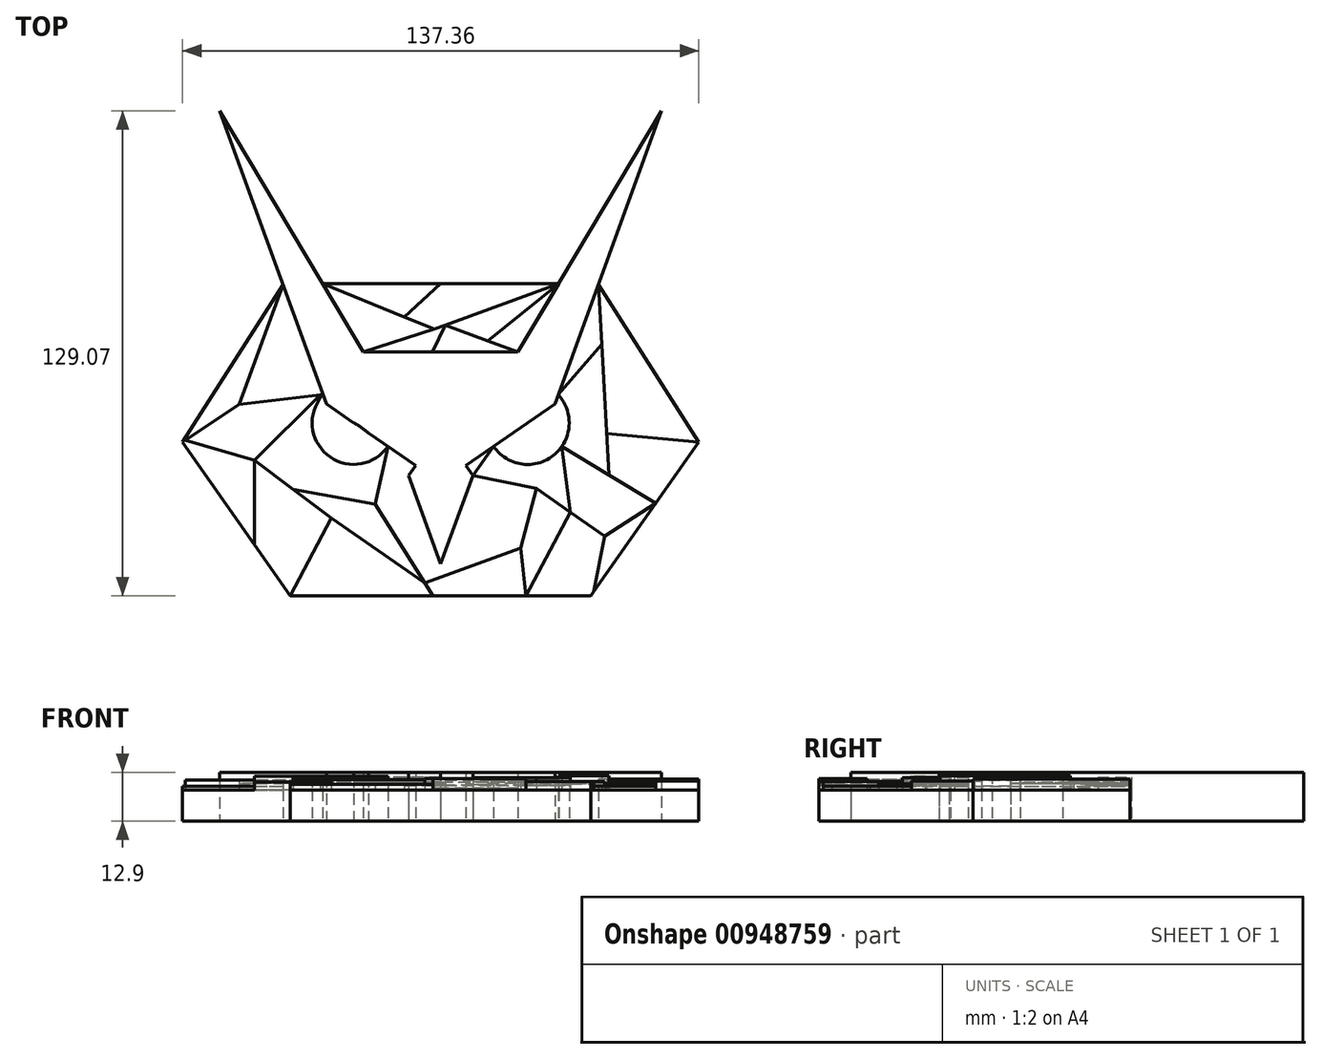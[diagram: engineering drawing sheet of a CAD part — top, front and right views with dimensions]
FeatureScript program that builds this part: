
annotation { "Feature Type Name" : "Feature", "Feature Type Description" : "" }
export const myFeature = defineFeature(function(context is Context, id is Id, definition is map)
    precondition{}
    {
        {
            var Q0;
            Q0=qCreatedBy(makeId("Top.planeOp"),FACE);
            var sketch = newSketch(context, id + "F0", { "sketchPlane" : qUnion([Q0])});
            skLineSegment(sketch, "E0", {"start": v(-40.57, 106.01) * mm, "end": v(-40.57, -104.1) * mm});
            skLineSegment(sketch, "E1", {"start": v(-40.57, 0) * mm, "end": v(-80.57, 0) * mm});
            skPoint(sketch, "E1.startSnap0", {"position": v(-40.57, 0.95) * mm});
            skLineSegment(sketch, "E2", {"start": v(-80.57, 0) * mm, "end": v(-109.25, 40.96) * mm});
            skLineSegment(sketch, "E3", {"start": v(-109.25, 40.96) * mm, "end": v(-82.39, 83.13) * mm});
            skLineSegment(sketch, "E4.MirrorCS", {"start": v(-40.57, 0) * mm, "end": v(-0.57, 0) * mm});
            skLineSegment(sketch, "E5.MirrorCS", {"start": v(-0.57, 0) * mm, "end": v(28.1, 40.96) * mm});
            skLineSegment(sketch, "E6.MirrorCS", {"start": v(28.1, 40.96) * mm, "end": v(1.24, 83.13) * mm});
            skLineSegment(sketch, "E7", {"start": v(-40.57, 0) * mm, "end": v(-40.57, 8.54) * mm});
            skLineSegment(sketch, "E8", {"start": v(-40.57, 8.54) * mm, "end": v(-49.12, 32.03) * mm});
            skLineSegment(sketch, "E9", {"start": v(-49.12, 32.03) * mm, "end": v(-45.4, 37.35) * mm});
            skLineSegment(sketch, "E10", {"start": v(-47.26, 34.7) * mm, "end": v(-71, 51.04) * mm});
            skLineSegment(sketch, "E11", {"start": v(-71, 51.04) * mm, "end": v(-99.4, 129.07) * mm});
            skLineSegment(sketch, "E12", {"start": v(-99.4, 129.07) * mm, "end": v(-61.13, 64.93) * mm});
            skLineSegment(sketch, "E13", {"start": v(-61.13, 64.93) * mm, "end": v(-40.57, 64.93) * mm});
            skLineSegment(sketch, "E14", {"start": v(-47.26, 34.7) * mm, "end": v(-59.61, 43.2) * mm});
            skLineSegment(sketch, "E15", {"start": v(-59.61, 43.2) * mm, "end": v(-63.73, 46.04) * mm});
            skFitSpline(sketch, "E16", {"points": [v(-63.73, 46.04) * mm, v(-55.85, 40.6) * mm], "startDerivative": vector(8.61, -4.18) * mm, "endDerivative": vector(8.61, -4.18) * mm});
            skArc(sketch, "E17", {"start": v(-72.82, 52.3) * mm, "mid": v(-70, 36.95) * mm, "end": v(-54.64, 39.77) * mm});
            skLineSegment(sketch, "E18", {"start": v(-71.99, 83.13) * mm, "end": v(-40.57, 83.13) * mm});
            skLineSegment(sketch, "E19", {"start": v(-72.82, 52.3) * mm, "end": v(-71.93, 53.6) * mm});
            skLineSegment(sketch, "E20.MirrorCS", {"start": v(-20.02, 64.93) * mm, "end": v(-40.57, 64.93) * mm});
            skLineSegment(sketch, "E21.MirrorCS", {"start": v(18.25, 129.07) * mm, "end": v(-20.02, 64.93) * mm});
            skLineSegment(sketch, "E22.MirrorCS", {"start": v(-9.16, 83.13) * mm, "end": v(-40.57, 83.13) * mm});
            skLineSegment(sketch, "E23.MirrorCS", {"start": v(-10.15, 51.04) * mm, "end": v(18.25, 129.07) * mm});
            skLineSegment(sketch, "E24.MirrorCS", {"start": v(-33.89, 34.7) * mm, "end": v(-10.15, 51.04) * mm});
            skArc(sketch, "E25.MirrorCS", {"start": v(-8.33, 52.3) * mm, "mid": v(-11.15, 36.95) * mm, "end": v(-26.5, 39.77) * mm});
            skLineSegment(sketch, "E26.MirrorCS", {"start": v(-8.33, 52.3) * mm, "end": v(-9.22, 53.6) * mm});
            skLineSegment(sketch, "E27.MirrorCS", {"start": v(-32.02, 32.03) * mm, "end": v(-35.75, 37.35) * mm});
            skLineSegment(sketch, "E28.MirrorCS", {"start": v(-40.57, 8.54) * mm, "end": v(-32.02, 32.03) * mm});
            skSolve(sketch);
        }
        {
            var Q0;
            {var subQ5=sQuery(id+"F0.wireOp",EDGE,"E1");Q0=makeQuery(id+"F0.imprint","IMPRINT",FACE,{"disambiguationData":[TD([[makeQuery(id+"F0.imprint","IMPRINT",EDGE,{"derivedFrom":subQ5}),-1.0]])]});}
            var Q1;
            {var subQ4=sQuery(id+"F0.wireOp",EDGE,"E4.MirrorCS");Q1=makeQuery(id+"F0.imprint","IMPRINT",FACE,{"disambiguationData":[TD([[makeQuery(id+"F0.imprint","IMPRINT",EDGE,{"derivedFrom":subQ4}),1.0]])]});}
            var Q2;
            {var subQ0=sQuery(id+"F0.wireOp",EDGE,"E20.MirrorCS");Q2=makeQuery(id+"F0.imprint","IMPRINT",FACE,{"disambiguationData":[TD([[makeQuery(id+"F0.imprint","IMPRINT",EDGE,{"derivedFrom":subQ0}),-1.0]])]});}
            var Q3;
            {var subQ0=sQuery(id+"F0.wireOp",EDGE,"E13");Q3=makeQuery(id+"F0.imprint","IMPRINT",FACE,{"disambiguationData":[TD([[makeQuery(id+"F0.imprint","IMPRINT",EDGE,{"derivedFrom":subQ0}),1.0]])]});}
            extrude(context, id + "F1", {"entities" : qUnion([Q0, Q1, Q2, Q3]), "depth" : 8.3 * mm, "offsetDistance" : 25 * mm});
        }
        {
            var Q0;
            {var subQ14=sQuery(id+"F0.wireOp",EDGE,"E8");Q0=makeQuery(id+"F0.imprint","IMPRINT",FACE,{"disambiguationData":[TD([[makeQuery(id+"F0.imprint","IMPRINT",EDGE,{"derivedFrom":subQ14}),-1.0]])]});}
            var Q1;
            {var subQ12=sQuery(id+"F0.wireOp",EDGE,"E20.MirrorCS");Q1=makeQuery(id+"F0.imprint","IMPRINT",FACE,{"disambiguationData":[TD([[makeQuery(id+"F0.imprint","IMPRINT",EDGE,{"derivedFrom":subQ12}),1.0]])]});}
            extrude(context, id + "F2", {"entities" : qUnion([Q0, Q1]), "depth" : 12.9 * mm, "offsetDistance" : 25 * mm});
        }
        {
            var Q0;
            Q0=makeQuery(id+"F1.opExtrude","CAP_FACE",FACE,{"disambiguationData":[OSD([sQuery(id+"F0.wireOp",EDGE,"E1"),sQuery(id+"F0.wireOp",EDGE,"E2"),sQuery(id+"F0.wireOp",EDGE,"E3"),sQuery(id+"F0.wireOp",EDGE,"E4.MirrorCS"),sQuery(id+"F0.wireOp",EDGE,"E5.MirrorCS"),sQuery(id+"F0.wireOp",EDGE,"E6.MirrorCS"),sQuery(id+"F0.wireOp",EDGE,"E8"),sQuery(id+"F0.wireOp",EDGE,"E9"),sQuery(id+"F0.wireOp",EDGE,"E10"),sQuery(id+"F0.wireOp",EDGE,"E11"),sQuery(id+"F0.wireOp",EDGE,"E17"),sQuery(id+"F0.wireOp",EDGE,"E19"),sQuery(id+"F0.wireOp",EDGE,"E23.MirrorCS"),sQuery(id+"F0.wireOp",EDGE,"E24.MirrorCS"),sQuery(id+"F0.wireOp",EDGE,"E25.MirrorCS"),sQuery(id+"F0.wireOp",EDGE,"E26.MirrorCS"),sQuery(id+"F0.wireOp",EDGE,"E27.MirrorCS"),sQuery(id+"F0.wireOp",EDGE,"E28.MirrorCS")])],"isStart":false});
            var sketch = newSketch(context, id + "F3", { "sketchPlane" : qUnion([Q0])});
            skLineSegment(sketch, "E29", {"start": v(-80.57, 0) * mm, "end": v(-69.7, 20.68) * mm});
            skLineSegment(sketch, "E30", {"start": v(-69.7, 20.68) * mm, "end": v(-90.08, 36.07) * mm});
            skLineSegment(sketch, "E31", {"start": v(-71.93, 53.6) * mm, "end": v(-94.27, 50.91) * mm});
            skLineSegment(sketch, "E32", {"start": v(-94.27, 50.91) * mm, "end": v(-82.57, 82.84) * mm});
            skLineSegment(sketch, "E33", {"start": v(-94.27, 50.91) * mm, "end": v(-108.58, 41.4) * mm});
            skLineSegment(sketch, "E34", {"start": v(-90.08, 36.07) * mm, "end": v(-90.08, 13.58) * mm});
            skLineSegment(sketch, "E35", {"start": v(-79.9, 28.37) * mm, "end": v(-58.07, 24.4) * mm});
            skLineSegment(sketch, "E36", {"start": v(-58.07, 24.4) * mm, "end": v(-54.64, 39.77) * mm});
            skLineSegment(sketch, "E37", {"start": v(-58.07, 24.4) * mm, "end": v(-42.67, 0) * mm});
            skLineSegment(sketch, "E38", {"start": v(-69.7, 20.68) * mm, "end": v(-44.85, 3.46) * mm});
            skLineSegment(sketch, "E39", {"start": v(-44.85, 3.46) * mm, "end": v(-19.23, 12.78) * mm});
            skLineSegment(sketch, "E40", {"start": v(-19.23, 12.78) * mm, "end": v(-15.06, 28.57) * mm});
            skLineSegment(sketch, "E41", {"start": v(-15.06, 28.57) * mm, "end": v(-32.02, 32.03) * mm});
            skLineSegment(sketch, "E42", {"start": v(-32.02, 32.03) * mm, "end": v(-26.5, 39.77) * mm});
            skLineSegment(sketch, "E43", {"start": v(-15.06, 28.57) * mm, "end": v(3.04, 15.9) * mm});
            skLineSegment(sketch, "E44", {"start": v(3.04, 15.9) * mm, "end": v(16.68, 24.64) * mm});
            skLineSegment(sketch, "E45", {"start": v(16.68, 24.64) * mm, "end": v(-8.33, 39.77) * mm});
            skLineSegment(sketch, "E46", {"start": v(-8.33, 39.77) * mm, "end": v(-6, 22.23) * mm});
            skLineSegment(sketch, "E47", {"start": v(4.18, 32.2) * mm, "end": v(1.43, 82.84) * mm});
            skLineSegment(sketch, "E48", {"start": v(3.58, 43.24) * mm, "end": v(28.1, 40.96) * mm});
            skLineSegment(sketch, "E49", {"start": v(2.3, 66.9) * mm, "end": v(-9.22, 53.6) * mm});
            skLineSegment(sketch, "E50", {"start": v(3.04, 15.9) * mm, "end": v(0, 0) * mm});
            skLineSegment(sketch, "E51", {"start": v(-6, 22.23) * mm, "end": v(-17.88, 0) * mm});
            skLineSegment(sketch, "E52", {"start": v(-17.88, 0) * mm, "end": v(-19.23, 12.78) * mm});
            skLineSegment(sketch, "E53", {"start": v(-90.08, 36.07) * mm, "end": v(-108.58, 41.4) * mm});
            skLineSegment(sketch, "E54", {"start": v(-90.08, 36.07) * mm, "end": v(-72.62, 53.51) * mm});
            skSolve(sketch);
        }
        {
            var Q0;
            {var subQ3=sQuery(id+"F3.wireOp",EDGE,"E29");Q0=makeQuery(id+"F3.imprint","IMPRINT",FACE,{"disambiguationData":[TD([[makeQuery(id+"F3.imprint","IMPRINT",EDGE,{"derivedFrom":subQ3}),1.0]])]});}
            extrude(context, id + "F4", {"entities" : qUnion([Q0]), "operationType" : NewBodyOperationType.ADD, "depth" : 2.1 * mm, "offsetDistance" : 25 * mm});
        }
        {
            var Q0;
            Q0=makeQuery(id+"F3.imprint","IMPRINT",FACE,{"disambiguationData":[TD([[makeQuery(id+"F3.imprint","IMPRINT",EDGE,{"derivedFrom":sQuery(id+"F3.wireOp",EDGE,"E31")}),-1.0]])]});
            extrude(context, id + "F5", {"entities" : qUnion([Q0]), "depth" : 1.7 * mm, "offsetDistance" : 25 * mm});
        }
        {
            var Q0;
            Q0=makeQuery(id+"F3.imprint","IMPRINT",FACE,{"disambiguationData":[TD([[makeQuery(id+"F3.imprint","IMPRINT",EDGE,{"derivedFrom":sQuery(id+"F3.wireOp",EDGE,"E32")}),1.0]])]});
            extrude(context, id + "F6", {"entities" : qUnion([Q0]), "depth" : 0.9 * mm, "offsetDistance" : 25 * mm});
        }
        {
            var Q0;
            {var subQ0=sQuery(id+"F3.wireOp",EDGE,"E33");Q0=makeQuery(id+"F3.imprint","IMPRINT",FACE,{"disambiguationData":[TD([[makeQuery(id+"F3.imprint","IMPRINT",EDGE,{"derivedFrom":subQ0}),1.0]])]});}
            extrude(context, id + "F7", {"entities" : qUnion([Q0]), "depth" : 2.6 * mm, "offsetDistance" : 25 * mm});
        }
        {
            var Q0;
            {var subQ0=sQuery(id+"F3.wireOp",EDGE,"E35");Q0=makeQuery(id+"F3.imprint","IMPRINT",FACE,{"disambiguationData":[TD([[makeQuery(id+"F3.imprint","IMPRINT",EDGE,{"derivedFrom":subQ0}),1.0]])]});}
            extrude(context, id + "F8", {"entities" : qUnion([Q0]), "depth" : 3.6 * mm, "offsetDistance" : 25 * mm});
        }
        {
            var Q0;
            {var subQ2=sQuery(id+"F3.wireOp",EDGE,"E35");Q0=makeQuery(id+"F3.imprint","IMPRINT",FACE,{"disambiguationData":[TD([[makeQuery(id+"F3.imprint","IMPRINT",EDGE,{"derivedFrom":subQ2}),-1.0]])]});}
            extrude(context, id + "F9", {"entities" : qUnion([Q0]), "depth" : 2.7 * mm, "offsetDistance" : 25 * mm});
        }
        {
            var Q0;
            {var subQ0=sQuery(id+"F3.wireOp",EDGE,"E29");Q0=makeQuery(id+"F3.imprint","IMPRINT",FACE,{"disambiguationData":[TD([[makeQuery(id+"F3.imprint","IMPRINT",EDGE,{"derivedFrom":subQ0}),-1.0]])]});}
            extrude(context, id + "F10", {"entities" : qUnion([Q0]), "depth" : 1.5 * mm, "offsetDistance" : 25 * mm});
        }
        {
            var Q0;
            {var subQ2=sQuery(id+"F3.wireOp",EDGE,"E36");Q0=makeQuery(id+"F3.imprint","IMPRINT",FACE,{"disambiguationData":[TD([[makeQuery(id+"F3.imprint","IMPRINT",EDGE,{"derivedFrom":subQ2}),-1.0]])]});}
            extrude(context, id + "F11", {"entities" : qUnion([Q0]), "depth" : 2.1 * mm, "offsetDistance" : 25 * mm});
        }
        {
            var Q0;
            {var subQ3=sQuery(id+"F3.wireOp",EDGE,"E39");Q0=makeQuery(id+"F3.imprint","IMPRINT",FACE,{"disambiguationData":[TD([[makeQuery(id+"F3.imprint","IMPRINT",EDGE,{"derivedFrom":subQ3}),-1.0]])]});}
            extrude(context, id + "F12", {"entities" : qUnion([Q0]), "depth" : 3 * mm, "offsetDistance" : 25 * mm});
        }
        {
            var Q0;
            {var subQ0=sQuery(id+"F3.wireOp",EDGE,"E40");Q0=makeQuery(id+"F3.imprint","IMPRINT",FACE,{"disambiguationData":[TD([[makeQuery(id+"F3.imprint","IMPRINT",EDGE,{"derivedFrom":subQ0}),-1.0]])]});}
            extrude(context, id + "F13", {"entities" : qUnion([Q0]), "depth" : 1.2 * mm, "offsetDistance" : 25 * mm});
        }
        {
            var Q0;
            {var subQ4=sQuery(id+"F3.wireOp",EDGE,"E41");Q0=makeQuery(id+"F3.imprint","IMPRINT",FACE,{"disambiguationData":[TD([[makeQuery(id+"F3.imprint","IMPRINT",EDGE,{"derivedFrom":subQ4}),-1.0]])]});}
            extrude(context, id + "F14", {"entities" : qUnion([Q0]), "depth" : 3.2 * mm, "offsetDistance" : 25 * mm});
        }
        {
            var Q0;
            Q0=makeQuery(id+"F3.imprint","IMPRINT",FACE,{"disambiguationData":[TD([[makeQuery(id+"F3.imprint","IMPRINT",EDGE,{"derivedFrom":sQuery(id+"F3.wireOp",EDGE,"E42")}),1.0]])]});
            extrude(context, id + "F15", {"entities" : qUnion([Q0]), "depth" : 1.5 * mm, "offsetDistance" : 25 * mm});
        }
        {
            var Q0;
            {var subQ3=sQuery(id+"F3.wireOp",EDGE,"E51");Q0=makeQuery(id+"F3.imprint","IMPRINT",FACE,{"disambiguationData":[TD([[makeQuery(id+"F3.imprint","IMPRINT",EDGE,{"derivedFrom":subQ3}),1.0]])]});}
            extrude(context, id + "F16", {"entities" : qUnion([Q0]), "depth" : 2.2 * mm, "offsetDistance" : 25 * mm});
        }
        {
            var Q0;
            {var subQ3=sQuery(id+"F3.wireOp",EDGE,"E44");Q0=makeQuery(id+"F3.imprint","IMPRINT",FACE,{"disambiguationData":[TD([[makeQuery(id+"F3.imprint","IMPRINT",EDGE,{"derivedFrom":subQ3}),1.0]])]});}
            extrude(context, id + "F17", {"entities" : qUnion([Q0]), "depth" : 1.6 * mm, "offsetDistance" : 25 * mm});
        }
        {
            var Q0;
            {var subQ0=sQuery(id+"F3.wireOp",EDGE,"E44");Q0=makeQuery(id+"F3.imprint","IMPRINT",FACE,{"disambiguationData":[TD([[makeQuery(id+"F3.imprint","IMPRINT",EDGE,{"derivedFrom":subQ0}),-1.0]])]});}
            extrude(context, id + "F18", {"entities" : qUnion([Q0]), "depth" : 1 * mm, "offsetDistance" : 25 * mm});
        }
        {
            var Q0;
            {var subQ0=sQuery(id+"F3.wireOp",EDGE,"E49");Q0=makeQuery(id+"F3.imprint","IMPRINT",FACE,{"disambiguationData":[TD([[makeQuery(id+"F3.imprint","IMPRINT",EDGE,{"derivedFrom":subQ0}),1.0]])]});}
            extrude(context, id + "F19", {"entities" : qUnion([Q0]), "depth" : 3.7 * mm, "offsetDistance" : 25 * mm});
        }
        {
            var Q0;
            {var subQ5=sQuery(id+"F3.wireOp",EDGE,"E48");Q0=makeQuery(id+"F3.imprint","IMPRINT",FACE,{"disambiguationData":[TD([[makeQuery(id+"F3.imprint","IMPRINT",EDGE,{"derivedFrom":subQ5}),-1.0]])]});}
            extrude(context, id + "F20", {"entities" : qUnion([Q0]), "depth" : 2.4 * mm, "offsetDistance" : 25 * mm});
        }
        {
            var Q0;
            {var subQ0=sQuery(id+"F3.wireOp",EDGE,"E48");Q0=makeQuery(id+"F3.imprint","IMPRINT",FACE,{"disambiguationData":[TD([[makeQuery(id+"F3.imprint","IMPRINT",EDGE,{"derivedFrom":subQ0}),1.0]])]});}
            extrude(context, id + "F21", {"entities" : qUnion([Q0]), "depth" : 2.9 * mm, "offsetDistance" : 25 * mm});
        }
        {
            var Q0;
            {var subQ2=sQuery(id+"F3.wireOp",EDGE,"E49");Q0=makeQuery(id+"F3.imprint","IMPRINT",FACE,{"disambiguationData":[TD([[makeQuery(id+"F3.imprint","IMPRINT",EDGE,{"derivedFrom":subQ2}),-1.0]])]});}
            extrude(context, id + "F22", {"entities" : qUnion([Q0]), "depth" : 2.03 * mm, "offsetDistance" : 25 * mm});
        }
        {
            var Q0;
            Q0=makeQuery(id+"F1.opExtrude","CAP_FACE",FACE,{"disambiguationData":[OSD([sQuery(id+"F0.wireOp",EDGE,"E12"),sQuery(id+"F0.wireOp",EDGE,"E13"),sQuery(id+"F0.wireOp",EDGE,"E18"),sQuery(id+"F0.wireOp",EDGE,"E20.MirrorCS"),sQuery(id+"F0.wireOp",EDGE,"E21.MirrorCS"),sQuery(id+"F0.wireOp",EDGE,"E22.MirrorCS")])],"isStart":false});
            var sketch = newSketch(context, id + "F23", { "sketchPlane" : qUnion([Q0])});
            skLineSegment(sketch, "E55", {"start": v(-61.13, 64.93) * mm, "end": v(-39.3, 72) * mm});
            skLineSegment(sketch, "E56", {"start": v(-39.3, 72) * mm, "end": v(-20.02, 64.93) * mm});
            skLineSegment(sketch, "E57", {"start": v(-28.01, 67.86) * mm, "end": v(-9.16, 83.13) * mm});
            skLineSegment(sketch, "E58", {"start": v(-42.31, 71.02) * mm, "end": v(-71.99, 83.13) * mm});
            skLineSegment(sketch, "E59", {"start": v(-50.23, 74.25) * mm, "end": v(-40.57, 83.13) * mm});
            skLineSegment(sketch, "E60", {"start": v(-39.3, 72) * mm, "end": v(-9.16, 83.13) * mm});
            skLineSegment(sketch, "E61", {"start": v(-39.3, 72) * mm, "end": v(-42.73, 64.93) * mm});
            skSolve(sketch);
        }
        {
            var Q0;
            {var subQ1=makeQuery(id+"F1.opExtrude","CAP_EDGE",EDGE,{"disambiguationData":[OSD([sQuery(id+"F0.wireOp",EDGE,"E12")])],"isStart":false});Q0=makeQuery(id+"F23.imprint","IMPRINT",FACE,{"disambiguationData":[TD([[makeQuery(id+"F23.imprint","IMPRINT",EDGE,{"derivedFrom":subQ1}),1.0]])]});}
            extrude(context, id + "F24", {"entities" : qUnion([Q0]), "depth" : 2.1 * mm, "offsetDistance" : 25 * mm});
        }
        {
            var Q0;
            {var subQ3=sQuery(id+"F23.wireOp",EDGE,"E59");Q0=makeQuery(id+"F23.imprint","IMPRINT",FACE,{"disambiguationData":[TD([[makeQuery(id+"F23.imprint","IMPRINT",EDGE,{"derivedFrom":subQ3}),1.0]])]});}
            extrude(context, id + "F25", {"entities" : qUnion([Q0]), "depth" : 3.4 * mm, "offsetDistance" : 25 * mm});
        }
        {
            var Q0;
            {var subQ1=sQuery(id+"F23.wireOp",EDGE,"E59");Q0=makeQuery(id+"F23.imprint","IMPRINT",FACE,{"disambiguationData":[TD([[makeQuery(id+"F23.imprint","IMPRINT",EDGE,{"derivedFrom":subQ1}),-1.0]])]});}
            extrude(context, id + "F26", {"entities" : qUnion([Q0]), "depth" : 1.2 * mm, "offsetDistance" : 25 * mm});
        }
        {
            var Q0;
            {var subQ4=sQuery(id+"F23.wireOp",EDGE,"E61");Q0=makeQuery(id+"F23.imprint","IMPRINT",FACE,{"disambiguationData":[TD([[makeQuery(id+"F23.imprint","IMPRINT",EDGE,{"derivedFrom":subQ4}),-1.0]])]});}
            extrude(context, id + "F27", {"entities" : qUnion([Q0]), "depth" : 1.6 * mm, "offsetDistance" : 25 * mm});
        }
        {
            var Q0;
            {var subQ0=sQuery(id+"F23.wireOp",EDGE,"E61");Q0=makeQuery(id+"F23.imprint","IMPRINT",FACE,{"disambiguationData":[TD([[makeQuery(id+"F23.imprint","IMPRINT",EDGE,{"derivedFrom":subQ0}),1.0]])]});}
            extrude(context, id + "F28", {"entities" : qUnion([Q0]), "depth" : 0.5 * mm, "offsetDistance" : 25 * mm});
        }
        {
            var Q0;
            {var subQ2=sQuery(id+"F23.wireOp",EDGE,"E57");Q0=makeQuery(id+"F23.imprint","IMPRINT",FACE,{"disambiguationData":[TD([[makeQuery(id+"F23.imprint","IMPRINT",EDGE,{"derivedFrom":subQ2}),1.0]])]});}
            extrude(context, id + "F29", {"entities" : qUnion([Q0]), "depth" : 2.6 * mm, "offsetDistance" : 25 * mm});
        }
        {
            var Q0;
            {var subQ2=sQuery(id+"F23.wireOp",EDGE,"E57");Q0=makeQuery(id+"F23.imprint","IMPRINT",FACE,{"disambiguationData":[TD([[makeQuery(id+"F23.imprint","IMPRINT",EDGE,{"derivedFrom":subQ2}),-1.0]])]});}
            extrude(context, id + "F30", {"entities" : qUnion([Q0]), "depth" : 1.9 * mm, "offsetDistance" : 25 * mm});
        }
    });
